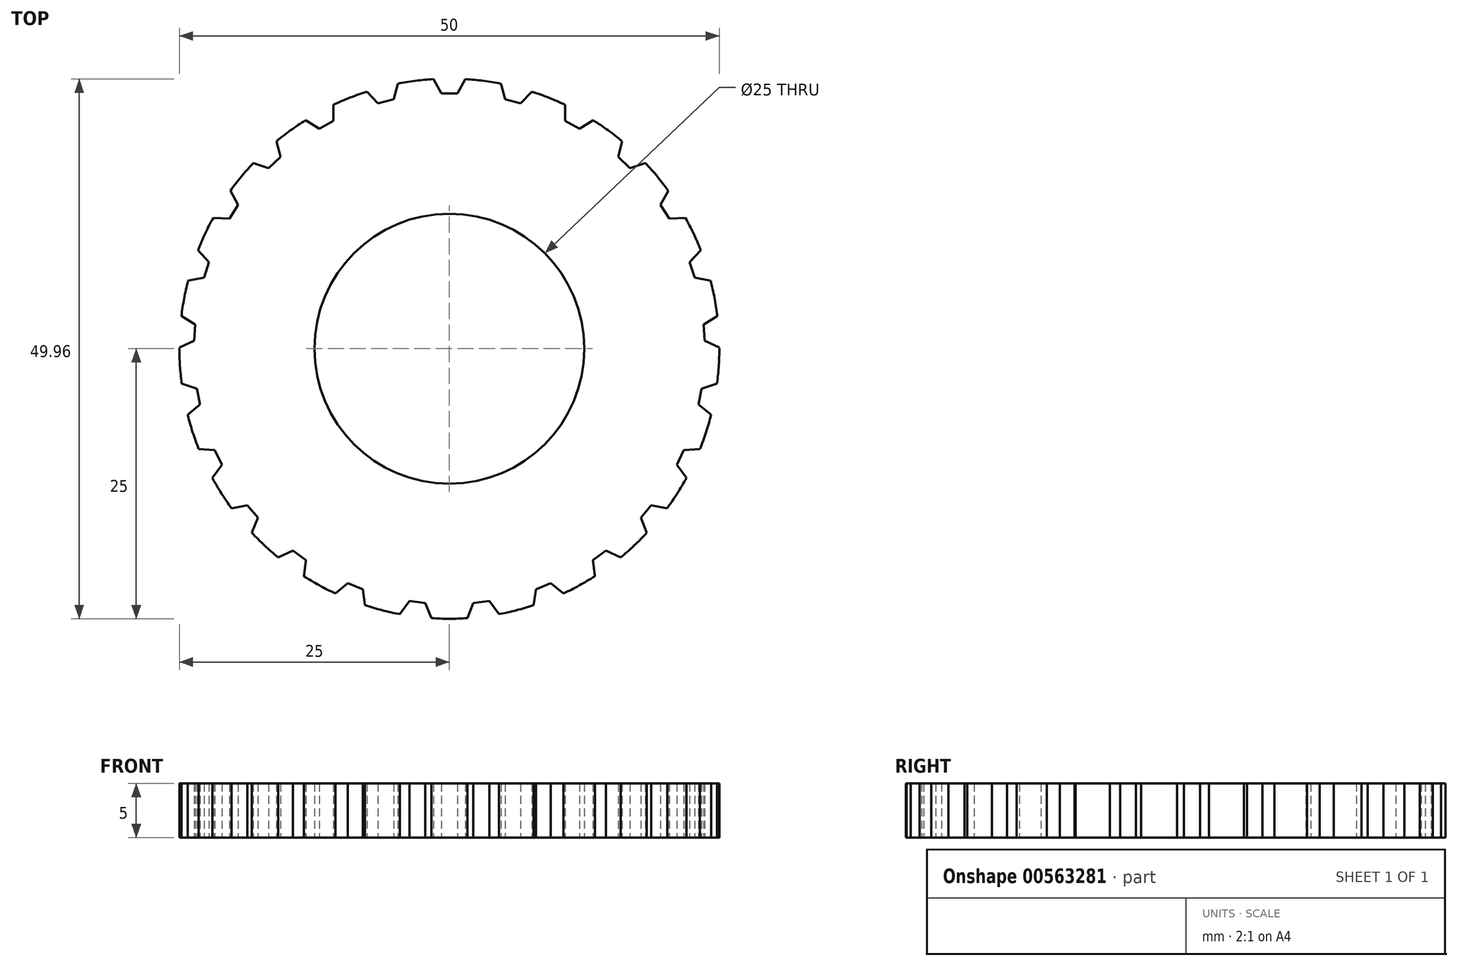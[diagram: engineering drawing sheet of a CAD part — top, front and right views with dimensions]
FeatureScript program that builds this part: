
annotation { "Feature Type Name" : "Feature", "Feature Type Description" : "" }
export const myFeature = defineFeature(function(context is Context, id is Id, definition is map)
    precondition{}
    {
        {
            var Q0;
            Q0=qCreatedBy(makeId("Top.planeOp"),FACE);
            var sketch = newSketch(context, id + "F0", { "sketchPlane" : qUnion([Q0])});
            skArc(sketch, "E0", {"start": v(-7.64, 23.8) * mm, "mid": v(-9.2, 23.24) * mm, "end": v(-10.73, 22.58) * mm});
            skCircle(sketch, "E1", {"center": v(0, 0) * mm, "radius": 12.5 * mm});
            skLineSegment(sketch, "E2", {"start": v(-1.48, 24.96) * mm, "end": v(-0.75, 23.64) * mm});
            skLineSegment(sketch, "E3", {"start": v(-0.75, 23.64) * mm, "end": v(0.75, 23.64) * mm});
            skLineSegment(sketch, "E4", {"start": v(0.75, 23.64) * mm, "end": v(1.48, 24.96) * mm});
            skLineSegment(sketch, "E5.1.0", {"start": v(-7.64, 23.8) * mm, "end": v(-6.6, 22.72) * mm});
            skLineSegment(sketch, "E5.1.1", {"start": v(-6.6, 22.72) * mm, "end": v(-5.15, 23.09) * mm});
            skLineSegment(sketch, "E5.1.2", {"start": v(-5.15, 23.09) * mm, "end": v(-4.78, 24.54) * mm});
            skLineSegment(sketch, "E5.2.0", {"start": v(-13.32, 21.16) * mm, "end": v(-12.05, 20.36) * mm});
            skLineSegment(sketch, "E5.2.1", {"start": v(-12.05, 20.36) * mm, "end": v(-10.73, 21.08) * mm});
            skLineSegment(sketch, "E5.2.2", {"start": v(-10.73, 21.08) * mm, "end": v(-10.73, 22.58) * mm});
            skLineSegment(sketch, "E6.2.3.0", {"start": v(-18.16, 17.18) * mm, "end": v(-16.73, 16.72) * mm});
            skLineSegment(sketch, "E6.3.3.0", {"start": v(-16.73, 16.72) * mm, "end": v(-15.64, 17.75) * mm});
            skLineSegment(sketch, "E6.6.3.0", {"start": v(-15.64, 17.75) * mm, "end": v(-16, 19.2) * mm});
            skLineSegment(sketch, "E6.2.4.0", {"start": v(-21.86, 12.13) * mm, "end": v(-20.37, 12.04) * mm});
            skLineSegment(sketch, "E6.3.4.0", {"start": v(-20.37, 12.04) * mm, "end": v(-19.56, 13.3) * mm});
            skLineSegment(sketch, "E6.6.4.0", {"start": v(-19.56, 13.3) * mm, "end": v(-20.28, 14.62) * mm});
            skLineSegment(sketch, "E6.2.5.0", {"start": v(-24.2, 6.3) * mm, "end": v(-22.72, 6.6) * mm});
            skLineSegment(sketch, "E6.3.5.0", {"start": v(-22.72, 6.6) * mm, "end": v(-22.26, 8.02) * mm});
            skLineSegment(sketch, "E6.6.5.0", {"start": v(-22.26, 8.02) * mm, "end": v(-23.28, 9.12) * mm});
            skLineSegment(sketch, "E6.2.6.0", {"start": v(-25, 0.1) * mm, "end": v(-23.64, 0.74) * mm});
            skLineSegment(sketch, "E6.3.6.0", {"start": v(-23.64, 0.74) * mm, "end": v(-23.55, 2.23) * mm});
            skLineSegment(sketch, "E6.6.6.0", {"start": v(-23.55, 2.23) * mm, "end": v(-24.81, 3.04) * mm});
            skLineSegment(sketch, "E6.2.7.0", {"start": v(-24.24, -6.13) * mm, "end": v(-23.09, -5.17) * mm});
            skLineSegment(sketch, "E6.3.7.0", {"start": v(-23.09, -5.17) * mm, "end": v(-23.37, -3.7) * mm});
            skLineSegment(sketch, "E6.6.7.0", {"start": v(-23.37, -3.7) * mm, "end": v(-24.8, -3.23) * mm});
            skLineSegment(sketch, "E6.2.8.0", {"start": v(-21.95, -11.96) * mm, "end": v(-21.07, -10.75) * mm});
            skLineSegment(sketch, "E6.3.8.0", {"start": v(-21.07, -10.75) * mm, "end": v(-21.71, -9.39) * mm});
            skLineSegment(sketch, "E6.6.8.0", {"start": v(-21.71, -9.39) * mm, "end": v(-23.21, -9.29) * mm});
            skLineSegment(sketch, "E6.2.9.0", {"start": v(-18.29, -17.05) * mm, "end": v(-17.74, -15.65) * mm});
            skLineSegment(sketch, "E6.3.9.0", {"start": v(-17.74, -15.65) * mm, "end": v(-18.7, -14.5) * mm});
            skLineSegment(sketch, "E6.6.9.0", {"start": v(-18.7, -14.5) * mm, "end": v(-20.17, -14.77) * mm});
            skLineSegment(sketch, "E6.2.10.0", {"start": v(-13.47, -21.06) * mm, "end": v(-13.3, -19.57) * mm});
            skLineSegment(sketch, "E6.3.10.0", {"start": v(-13.3, -19.57) * mm, "end": v(-14.5, -18.69) * mm});
            skLineSegment(sketch, "E6.6.10.0", {"start": v(-14.5, -18.69) * mm, "end": v(-15.86, -19.32) * mm});
            skLineSegment(sketch, "E6.2.11.0", {"start": v(-7.81, -23.75) * mm, "end": v(-8, -22.26) * mm});
            skLineSegment(sketch, "E6.3.11.0", {"start": v(-8, -22.26) * mm, "end": v(-9.4, -21.7) * mm});
            skLineSegment(sketch, "E6.6.11.0", {"start": v(-9.4, -21.7) * mm, "end": v(-10.56, -22.66) * mm});
            skLineSegment(sketch, "E6.2.12.0", {"start": v(-1.66, -24.94) * mm, "end": v(-2.22, -23.55) * mm});
            skLineSegment(sketch, "E6.3.12.0", {"start": v(-2.22, -23.55) * mm, "end": v(-3.7, -23.36) * mm});
            skLineSegment(sketch, "E6.6.12.0", {"start": v(-3.7, -23.36) * mm, "end": v(-4.6, -24.57) * mm});
            skLineSegment(sketch, "E6.2.13.0", {"start": v(4.6, -24.57) * mm, "end": v(3.7, -23.36) * mm});
            skLineSegment(sketch, "E6.3.13.0", {"start": v(3.7, -23.36) * mm, "end": v(2.22, -23.55) * mm});
            skLineSegment(sketch, "E6.6.13.0", {"start": v(2.22, -23.55) * mm, "end": v(1.66, -24.94) * mm});
            skLineSegment(sketch, "E6.2.14.0", {"start": v(10.56, -22.66) * mm, "end": v(9.4, -21.7) * mm});
            skLineSegment(sketch, "E6.3.14.0", {"start": v(9.4, -21.7) * mm, "end": v(8, -22.26) * mm});
            skLineSegment(sketch, "E6.6.14.0", {"start": v(8, -22.26) * mm, "end": v(7.81, -23.75) * mm});
            skLineSegment(sketch, "E6.2.15.0", {"start": v(15.86, -19.32) * mm, "end": v(14.5, -18.69) * mm});
            skLineSegment(sketch, "E6.3.15.0", {"start": v(14.5, -18.69) * mm, "end": v(13.3, -19.57) * mm});
            skLineSegment(sketch, "E6.6.15.0", {"start": v(13.3, -19.57) * mm, "end": v(13.47, -21.06) * mm});
            skLineSegment(sketch, "E6.2.16.0", {"start": v(20.17, -14.77) * mm, "end": v(18.7, -14.5) * mm});
            skLineSegment(sketch, "E6.3.16.0", {"start": v(18.7, -14.5) * mm, "end": v(17.74, -15.65) * mm});
            skLineSegment(sketch, "E6.6.16.0", {"start": v(17.74, -15.65) * mm, "end": v(18.29, -17.05) * mm});
            skLineSegment(sketch, "E6.2.17.0", {"start": v(23.21, -9.29) * mm, "end": v(21.71, -9.39) * mm});
            skLineSegment(sketch, "E6.3.17.0", {"start": v(21.71, -9.39) * mm, "end": v(21.07, -10.75) * mm});
            skLineSegment(sketch, "E6.6.17.0", {"start": v(21.07, -10.75) * mm, "end": v(21.95, -11.96) * mm});
            skLineSegment(sketch, "E6.2.18.0", {"start": v(24.8, -3.23) * mm, "end": v(23.37, -3.7) * mm});
            skLineSegment(sketch, "E6.3.18.0", {"start": v(23.37, -3.7) * mm, "end": v(23.09, -5.17) * mm});
            skLineSegment(sketch, "E6.6.18.0", {"start": v(23.09, -5.17) * mm, "end": v(24.24, -6.13) * mm});
            skLineSegment(sketch, "E6.2.19.0", {"start": v(24.81, 3.04) * mm, "end": v(23.55, 2.23) * mm});
            skLineSegment(sketch, "E6.3.19.0", {"start": v(23.55, 2.23) * mm, "end": v(23.64, 0.74) * mm});
            skLineSegment(sketch, "E6.6.19.0", {"start": v(23.64, 0.74) * mm, "end": v(25, 0.1) * mm});
            skLineSegment(sketch, "E6.2.20.0", {"start": v(23.28, 9.12) * mm, "end": v(22.26, 8.02) * mm});
            skLineSegment(sketch, "E6.3.20.0", {"start": v(22.26, 8.02) * mm, "end": v(22.72, 6.6) * mm});
            skLineSegment(sketch, "E6.6.20.0", {"start": v(22.72, 6.6) * mm, "end": v(24.2, 6.3) * mm});
            skLineSegment(sketch, "E6.2.21.0", {"start": v(20.28, 14.62) * mm, "end": v(19.56, 13.3) * mm});
            skLineSegment(sketch, "E6.3.21.0", {"start": v(19.56, 13.3) * mm, "end": v(20.37, 12.04) * mm});
            skLineSegment(sketch, "E6.6.21.0", {"start": v(20.37, 12.04) * mm, "end": v(21.86, 12.13) * mm});
            skLineSegment(sketch, "E6.2.22.0", {"start": v(16, 19.2) * mm, "end": v(15.64, 17.75) * mm});
            skLineSegment(sketch, "E6.3.22.0", {"start": v(15.64, 17.75) * mm, "end": v(16.73, 16.72) * mm});
            skLineSegment(sketch, "E6.6.22.0", {"start": v(16.73, 16.72) * mm, "end": v(18.16, 17.18) * mm});
            skLineSegment(sketch, "E6.2.23.0", {"start": v(10.73, 22.58) * mm, "end": v(10.73, 21.08) * mm});
            skLineSegment(sketch, "E6.3.23.0", {"start": v(10.73, 21.08) * mm, "end": v(12.05, 20.36) * mm});
            skLineSegment(sketch, "E6.6.23.0", {"start": v(12.05, 20.36) * mm, "end": v(13.32, 21.16) * mm});
            skLineSegment(sketch, "E6.2.24.0", {"start": v(4.78, 24.54) * mm, "end": v(5.15, 23.09) * mm});
            skLineSegment(sketch, "E6.3.24.0", {"start": v(5.15, 23.09) * mm, "end": v(6.6, 22.72) * mm});
            skLineSegment(sketch, "E6.6.24.0", {"start": v(6.6, 22.72) * mm, "end": v(7.64, 23.8) * mm});
            skArc(sketch, "E7.trimOffspring", {"start": v(-1.48, 24.96) * mm, "mid": v(-3.13, 24.8) * mm, "end": v(-4.78, 24.54) * mm});
            skArc(sketch, "E8.trimOffspring", {"start": v(4.78, 24.54) * mm, "mid": v(3.13, 24.8) * mm, "end": v(1.48, 24.96) * mm});
            skArc(sketch, "E9.trimOffspring", {"start": v(10.73, 22.58) * mm, "mid": v(9.2, 23.24) * mm, "end": v(7.64, 23.8) * mm});
            skArc(sketch, "E10.trimOffspring", {"start": v(16, 19.2) * mm, "mid": v(14.7, 20.23) * mm, "end": v(13.32, 21.16) * mm});
            skArc(sketch, "E11.trimOffspring", {"start": v(20.28, 14.62) * mm, "mid": v(19.26, 15.94) * mm, "end": v(18.16, 17.18) * mm});
            skArc(sketch, "E12.trimOffspring", {"start": v(23.28, 9.12) * mm, "mid": v(22.62, 10.64) * mm, "end": v(21.86, 12.13) * mm});
            skArc(sketch, "E13.trimOffspring", {"start": v(24.81, 3.04) * mm, "mid": v(24.56, 4.68) * mm, "end": v(24.2, 6.3) * mm});
            skArc(sketch, "E14.trimOffspring", {"start": v(24.8, -3.23) * mm, "mid": v(24.95, -1.57) * mm, "end": v(25, 0.1) * mm});
            skArc(sketch, "E15.trimOffspring", {"start": v(23.21, -9.29) * mm, "mid": v(23.78, -7.73) * mm, "end": v(24.24, -6.13) * mm});
            skArc(sketch, "E16.trimOffspring", {"start": v(20.17, -14.77) * mm, "mid": v(21.1, -13.4) * mm, "end": v(21.95, -11.96) * mm});
            skArc(sketch, "E17.trimOffspring", {"start": v(15.86, -19.32) * mm, "mid": v(17.11, -18.22) * mm, "end": v(18.29, -17.05) * mm});
            skArc(sketch, "E18.trimOffspring", {"start": v(10.56, -22.66) * mm, "mid": v(12.04, -21.9) * mm, "end": v(13.47, -21.06) * mm});
            skArc(sketch, "E19.trimOffspring", {"start": v(4.6, -24.57) * mm, "mid": v(6.22, -24.21) * mm, "end": v(7.81, -23.75) * mm});
            skArc(sketch, "E20.trimOffspring", {"start": v(-1.66, -24.94) * mm, "mid": v(0, -25) * mm, "end": v(1.66, -24.94) * mm});
            skArc(sketch, "E21.trimOffspring", {"start": v(-7.81, -23.75) * mm, "mid": v(-6.22, -24.21) * mm, "end": v(-4.6, -24.57) * mm});
            skArc(sketch, "E22.trimOffspring", {"start": v(-13.47, -21.06) * mm, "mid": v(-12.04, -21.9) * mm, "end": v(-10.56, -22.66) * mm});
            skArc(sketch, "E23.trimOffspring", {"start": v(-18.29, -17.05) * mm, "mid": v(-17.11, -18.22) * mm, "end": v(-15.86, -19.32) * mm});
            skArc(sketch, "E24.trimOffspring", {"start": v(-21.95, -11.96) * mm, "mid": v(-21.1, -13.4) * mm, "end": v(-20.17, -14.77) * mm});
            skArc(sketch, "E25.trimOffspring", {"start": v(-24.24, -6.13) * mm, "mid": v(-23.78, -7.73) * mm, "end": v(-23.21, -9.29) * mm});
            skArc(sketch, "E26.trimOffspring", {"start": v(-25, 0.1) * mm, "mid": v(-24.95, -1.57) * mm, "end": v(-24.8, -3.23) * mm});
            skArc(sketch, "E27.trimOffspring", {"start": v(-24.2, 6.3) * mm, "mid": v(-24.56, 4.68) * mm, "end": v(-24.81, 3.04) * mm});
            skArc(sketch, "E28.trimOffspring", {"start": v(-21.86, 12.13) * mm, "mid": v(-22.62, 10.64) * mm, "end": v(-23.28, 9.12) * mm});
            skArc(sketch, "E29.trimOffspring", {"start": v(-18.16, 17.18) * mm, "mid": v(-19.26, 15.94) * mm, "end": v(-20.28, 14.62) * mm});
            skArc(sketch, "E30.trimOffspring", {"start": v(-13.32, 21.16) * mm, "mid": v(-14.7, 20.23) * mm, "end": v(-16, 19.2) * mm});
            skSolve(sketch);
        }
        {
            var Q0;
            Q0 = qSketchRegion(id + "F0", true);
            extrude(context, id + "F1", {"entities" : qUnion([Q0]), "depth" : 5 * mm, "offsetDistance" : 25 * mm});
        }
    });
